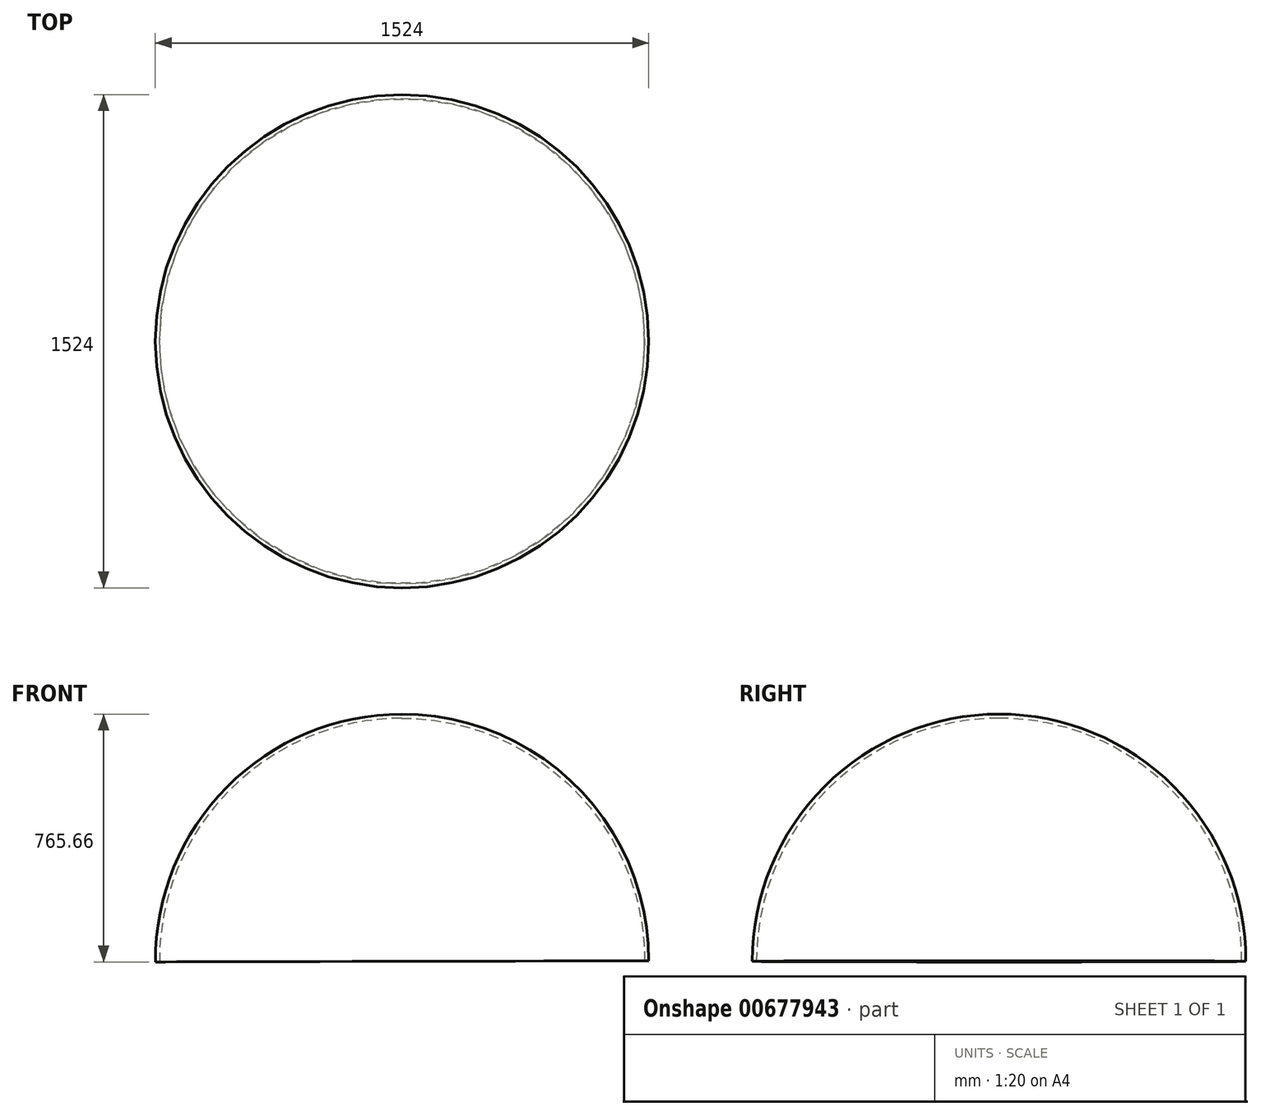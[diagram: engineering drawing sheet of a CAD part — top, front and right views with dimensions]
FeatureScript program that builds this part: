
annotation { "Feature Type Name" : "Feature", "Feature Type Description" : "" }
export const myFeature = defineFeature(function(context is Context, id is Id, definition is map)
    precondition{}
    {
        {
            var Q0;
            Q0=qCreatedBy(makeId("Front.planeOp"),FACE);
            var sketch = newSketch(context, id + "F0", { "sketchPlane" : qUnion([Q0])});
            skArc(sketch, "E0", {"start": v(762, 0) * mm, "mid": v(538.17, 539.46) * mm, "end": v(-1.83, 762) * mm});
            skArc(sketch, "E1.0", {"start": v(749.3, 0) * mm, "mid": v(529.19, 530.48) * mm, "end": v(-1.83, 749.3) * mm});
            skLineSegment(sketch, "E2", {"start": v(749.3, 0) * mm, "end": v(762, 0) * mm});
            skLineSegment(sketch, "E3", {"start": v(-1.83, 749.3) * mm, "end": v(-1.83, 762) * mm});
            skLineSegment(sketch, "E4", {"start": v(0, 0) * mm, "end": v(-1.83, 762) * mm});
            skSolve(sketch);
        }
        {
            var Q0;
            {var subQ0=sQuery(id+"F0.wireOp",EDGE,"E0");Q0=makeQuery(id+"F0.imprint","IMPRINT",FACE,{"disambiguationData":[TD([[makeQuery(id+"F0.imprint","IMPRINT",EDGE,{"derivedFrom":subQ0}),1.0]])]});}
            var Q1;
            Q1=sQuery(id+"F0.wireOp",EDGE,"E4");
            revolve(context, id + "F1", {"entities" : qUnion([Q0]), "axis" : qUnion([Q1]), "revolveType" : RevolveType.FULL});
        }
    });
